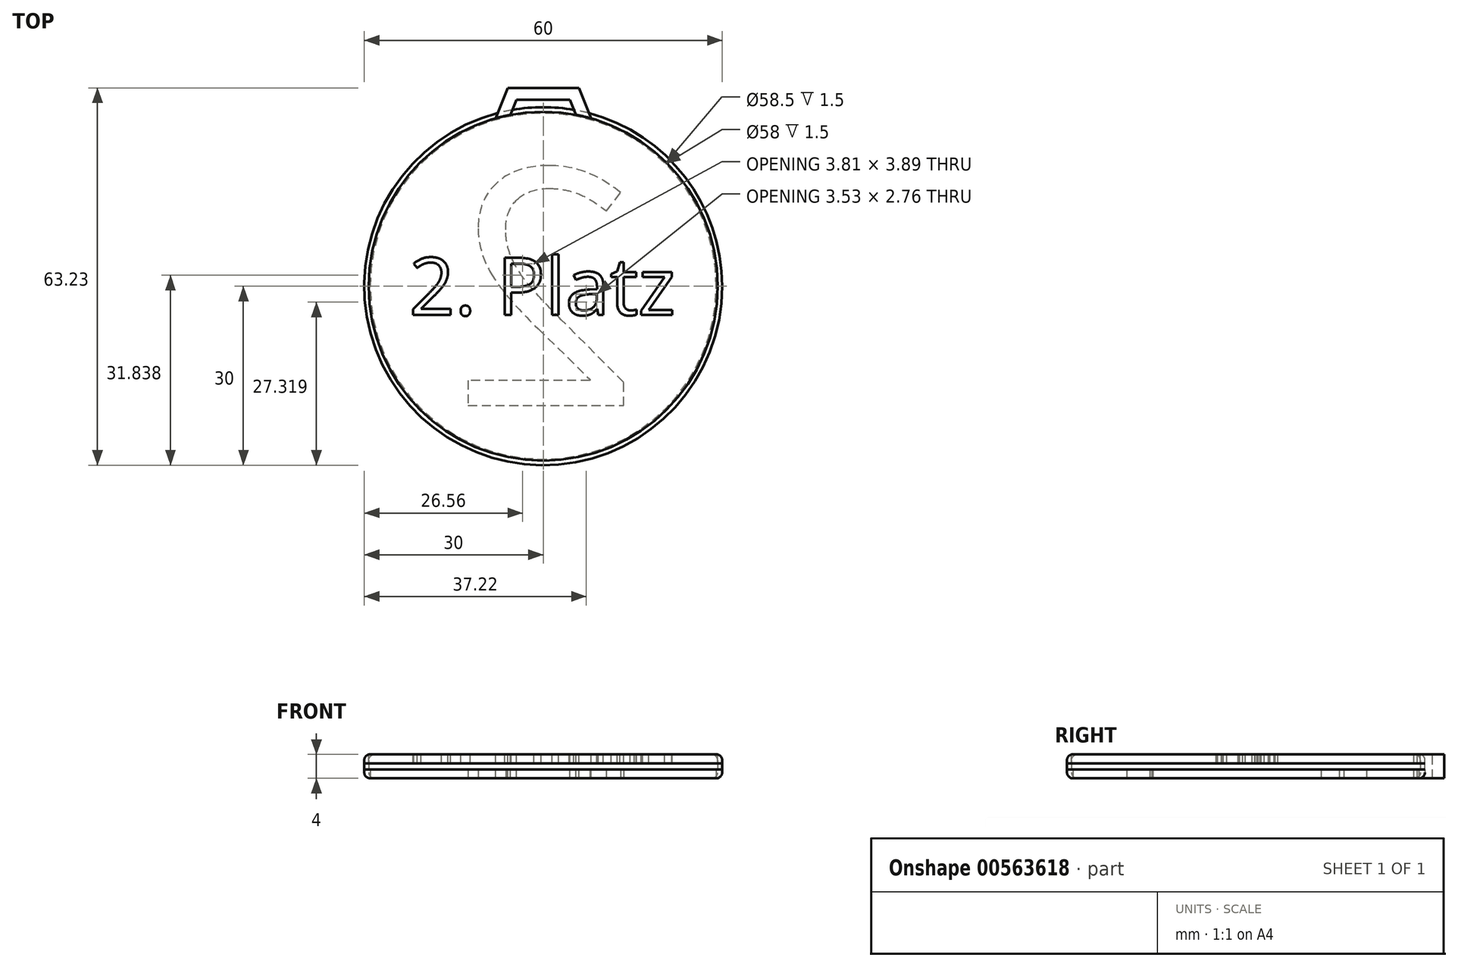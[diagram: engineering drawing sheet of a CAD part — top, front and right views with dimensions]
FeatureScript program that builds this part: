
annotation { "Feature Type Name" : "Feature", "Feature Type Description" : "" }
export const myFeature = defineFeature(function(context is Context, id is Id, definition is map)
    precondition{}
    {
        {
            var Q0;
            Q0=qCreatedBy(makeId("Top.planeOp"),FACE);
            var sketch = newSketch(context, id + "F0", { "sketchPlane" : qUnion([Q0])});
            skCircle(sketch, "E0", {"center": v(0, 0) * mm, "radius": 29.25 * mm});
            skSolve(sketch);
        }
        {
            var Q0;
            Q0 = qSketchRegion(id + "F0", true);
            extrude(context, id + "F1", {"entities" : qUnion([Q0]), "depth" : 4 * mm, "offsetDistance" : 25 * mm});
        }
        {
            var Q0;
            Q0=makeQuery(id+"F1.opExtrude","CAP_FACE",FACE,{"disambiguationData":[OSD([sQuery(id+"F0.wireOp",EDGE,"E0")])],"isStart":true});
            var sketch = newSketch(context, id + "F2", { "sketchPlane" : qUnion([Q0])});
            skText(sketch, "E1", { "text": "2", "fontName": "OpenSans-Regular.ttf"});
            skCircle(sketch, "E2", {"center": v(0, 0) * mm, "radius": 30 * mm});
            skCircle(sketch, "E3", {"center": v(0, 0) * mm, "radius": 29 * mm});
            const initialGuessF2  = {"E1": [-0.0162, -0.02, 1, 0, 0.04]};
            skSetInitialGuess(sketch, initialGuessF2);
            skSolve(sketch);
        }
        {
            var Q0;
            Q0 = qSketchRegion(id + "F2", true);
            var Q1;
            Q1=makeQuery(id+"F2.imprint","IMPRINT",FACE,{"disambiguationData":[TD([[makeQuery(id+"F2.imprint","IMPRINT",EDGE,{"derivedFrom":sQuery(id+"F2.wireOp",EDGE,"E1.sketch_text.stroke-0")}),-1.0]])]});
            extrude(context, id + "F3", {"entities" : qUnion([Q0, Q1]), "oppositeDirection" : true, "depth" : 1.5 * mm, "offsetDistance" : 25 * mm});
        }
        {
            var Q0;
            Q0=makeQuery(id+"F1.opExtrude","CAP_FACE",FACE,{"disambiguationData":[OSD([sQuery(id+"F0.wireOp",EDGE,"E0")])],"isStart":false});
            var sketch = newSketch(context, id + "F4", { "sketchPlane" : qUnion([Q0])});
            skText(sketch, "E4", { "text": "2. Platz", "fontName": "OpenSans-Regular.ttf"});
            skCircle(sketch, "E5", {"center": v(0, 0) * mm, "radius": 30 * mm});
            skCircle(sketch, "E6", {"center": v(0, 0) * mm, "radius": 29 * mm});
            const initialGuessF4  = {"E4": [-0.0225, -0.00483, 1, 0, 0.00966]};
            skSetInitialGuess(sketch, initialGuessF4);
            skSolve(sketch);
        }
        {
            var Q0;
            Q0=makeQuery(id+"F4.imprint","IMPRINT",FACE,{"disambiguationData":[TD([[makeQuery(id+"F4.imprint","IMPRINT",EDGE,{"derivedFrom":sQuery(id+"F4.wireOp",EDGE,"E4.sketch_text.stroke-0")}),-1.0]])]});
            var Q1;
            Q1=makeQuery(id+"F4.imprint","IMPRINT",FACE,{"disambiguationData":[TD([[makeQuery(id+"F4.imprint","IMPRINT",EDGE,{"derivedFrom":sQuery(id+"F4.wireOp",EDGE,"E4.sketch_text.stroke-20")}),-1.0]])]});
            var Q2;
            Q2=makeQuery(id+"F4.imprint","IMPRINT",FACE,{"disambiguationData":[TD([[makeQuery(id+"F4.imprint","IMPRINT",EDGE,{"derivedFrom":sQuery(id+"F4.wireOp",EDGE,"E4.sketch_text.stroke-28")}),-1.0]])]});
            var Q3;
            Q3=makeQuery(id+"F4.imprint","IMPRINT",FACE,{"disambiguationData":[TD([[makeQuery(id+"F4.imprint","IMPRINT",EDGE,{"derivedFrom":sQuery(id+"F4.wireOp",EDGE,"E4.sketch_text.stroke-43")}),-1.0]])]});
            var Q4;
            Q4=makeQuery(id+"F4.imprint","IMPRINT",FACE,{"disambiguationData":[TD([[makeQuery(id+"F4.imprint","IMPRINT",EDGE,{"derivedFrom":sQuery(id+"F4.wireOp",EDGE,"E4.sketch_text.stroke-47")}),-1.0]])]});
            var Q5;
            Q5=makeQuery(id+"F4.imprint","IMPRINT",FACE,{"disambiguationData":[TD([[makeQuery(id+"F4.imprint","IMPRINT",EDGE,{"derivedFrom":sQuery(id+"F4.wireOp",EDGE,"E4.sketch_text.stroke-74")}),-1.0]])]});
            var Q6;
            Q6=makeQuery(id+"F4.imprint","IMPRINT",FACE,{"disambiguationData":[TD([[makeQuery(id+"F4.imprint","IMPRINT",EDGE,{"derivedFrom":sQuery(id+"F4.wireOp",EDGE,"E4.sketch_text.stroke-93")}),-1.0]])]});
            var Q7;
            Q7=makeQuery(id+"F4.imprint","IMPRINT",FACE,{"disambiguationData":[TD([[makeQuery(id+"F4.imprint","IMPRINT",EDGE,{"derivedFrom":sQuery(id+"F4.wireOp",EDGE,"E5")}),1.0]])]});
            extrude(context, id + "F5", {"entities" : qUnion([Q0, Q1, Q2, Q3, Q4, Q5, Q6, Q7]), "oppositeDirection" : true, "depth" : 1.5 * mm, "offsetDistance" : 25 * mm});
        }
        {
            var Q0;
            Q0=qCreatedBy(makeId("Front.planeOp"),FACE);
            var sketch = newSketch(context, id + "F6", { "sketchPlane" : qUnion([Q0])});
            skLineSegment(sketch, "E7", {"start": v(0, 25) * mm, "end": v(0, -25) * mm, "construction": true});
            skSolve(sketch);
        }
        {
            var Q0;
            Q0=makeQuery(id+"F3.opExtrude","SWEPT_BODY",BODY,{"disambiguationData":[OSD([sQuery(id+"F2.wireOp",EDGE,"E1.sketch_text.stroke-0"),sQuery(id+"F2.wireOp",EDGE,"E1.sketch_text.stroke-1"),sQuery(id+"F2.wireOp",EDGE,"E1.sketch_text.stroke-2"),sQuery(id+"F2.wireOp",EDGE,"E1.sketch_text.stroke-3"),sQuery(id+"F2.wireOp",EDGE,"E1.sketch_text.stroke-4"),sQuery(id+"F2.wireOp",EDGE,"E1.sketch_text.stroke-5"),sQuery(id+"F2.wireOp",EDGE,"E1.sketch_text.stroke-6"),sQuery(id+"F2.wireOp",EDGE,"E1.sketch_text.stroke-7"),sQuery(id+"F2.wireOp",EDGE,"E1.sketch_text.stroke-8"),sQuery(id+"F2.wireOp",EDGE,"E1.sketch_text.stroke-9"),sQuery(id+"F2.wireOp",EDGE,"E1.sketch_text.stroke-10"),sQuery(id+"F2.wireOp",EDGE,"E1.sketch_text.stroke-11"),sQuery(id+"F2.wireOp",EDGE,"E1.sketch_text.stroke-12"),sQuery(id+"F2.wireOp",EDGE,"E1.sketch_text.stroke-13"),sQuery(id+"F2.wireOp",EDGE,"E1.sketch_text.stroke-14"),sQuery(id+"F2.wireOp",EDGE,"E1.sketch_text.stroke-15"),sQuery(id+"F2.wireOp",EDGE,"E1.sketch_text.stroke-16"),sQuery(id+"F2.wireOp",EDGE,"E1.sketch_text.stroke-17"),sQuery(id+"F2.wireOp",EDGE,"E1.sketch_text.stroke-18"),sQuery(id+"F2.wireOp",EDGE,"E1.sketch_text.stroke-19")])]});
            var Q1;
            Q1=sQuery(id+"F6.wireOp",EDGE,"E7");
            transform(context, id + "F7", {"entities" : qUnion([Q0]), "transformType" : TransformType.ROTATION, "transformAxis" : qUnion([Q1]), "angle" : 180 * degree, "makeCopy" : false});
        }
        {
            var Q0;
            Q0=makeQuery(id+"F5.opExtrude","CAP_FACE",FACE,{"disambiguationData":[OSD([sQuery(id+"F4.wireOp",EDGE,"E4.sketch_text.stroke-74"),sQuery(id+"F4.wireOp",EDGE,"E4.sketch_text.stroke-75"),sQuery(id+"F4.wireOp",EDGE,"E4.sketch_text.stroke-76"),sQuery(id+"F4.wireOp",EDGE,"E4.sketch_text.stroke-77"),sQuery(id+"F4.wireOp",EDGE,"E4.sketch_text.stroke-78"),sQuery(id+"F4.wireOp",EDGE,"E4.sketch_text.stroke-79"),sQuery(id+"F4.wireOp",EDGE,"E4.sketch_text.stroke-80"),sQuery(id+"F4.wireOp",EDGE,"E4.sketch_text.stroke-81"),sQuery(id+"F4.wireOp",EDGE,"E4.sketch_text.stroke-82"),sQuery(id+"F4.wireOp",EDGE,"E4.sketch_text.stroke-83"),sQuery(id+"F4.wireOp",EDGE,"E4.sketch_text.stroke-84"),sQuery(id+"F4.wireOp",EDGE,"E4.sketch_text.stroke-85"),sQuery(id+"F4.wireOp",EDGE,"E4.sketch_text.stroke-86"),sQuery(id+"F4.wireOp",EDGE,"E4.sketch_text.stroke-87"),sQuery(id+"F4.wireOp",EDGE,"E4.sketch_text.stroke-88"),sQuery(id+"F4.wireOp",EDGE,"E4.sketch_text.stroke-89"),sQuery(id+"F4.wireOp",EDGE,"E4.sketch_text.stroke-90"),sQuery(id+"F4.wireOp",EDGE,"E4.sketch_text.stroke-91"),sQuery(id+"F4.wireOp",EDGE,"E4.sketch_text.stroke-92")])],"isStart":false});
            var sketch = newSketch(context, id + "F8", { "sketchPlane" : qUnion([Q0])});
            skCircle(sketch, "E8", {"center": v(0, 0) * mm, "radius": 30 * mm});
            skSolve(sketch);
        }
        {
            var Q0;
            Q0 = qSketchRegion(id + "F8", true);
            extrude(context, id + "F9", {"entities" : qUnion([Q0]), "depth" : 1 * mm, "offsetDistance" : 25 * mm});
        }
        {
            var Q0;
            Q0=makeQuery(id+"F1.opExtrude","CAP_FACE",FACE,{"disambiguationData":[OSD([sQuery(id+"F0.wireOp",EDGE,"E0")])],"isStart":false});
            var sketch = newSketch(context, id + "F10", { "sketchPlane" : qUnion([Q0])});
            skLineSegment(sketch, "E9", {"start": v(-5.5, 28.73) * mm, "end": v(-4.5, 31.23) * mm});
            skLineSegment(sketch, "E10", {"start": v(-4.5, 31.23) * mm, "end": v(4.5, 31.23) * mm});
            skLineSegment(sketch, "E11", {"start": v(4.5, 31.23) * mm, "end": v(5.5, 28.73) * mm});
            skLineSegment(sketch, "E12", {"start": v(-8, 28.13) * mm, "end": v(-5.96, 33.23) * mm});
            skLineSegment(sketch, "E13", {"start": v(-5.96, 33.23) * mm, "end": v(5.96, 33.23) * mm});
            skLineSegment(sketch, "E14", {"start": v(5.96, 33.23) * mm, "end": v(8, 28.13) * mm});
            skArc(sketch, "E15", {"start": v(-8, 28.13) * mm, "mid": v(-6.76, 28.46) * mm, "end": v(-5.5, 28.73) * mm});
            skArc(sketch, "E16", {"start": v(5.5, 28.73) * mm, "mid": v(6.76, 28.46) * mm, "end": v(8, 28.13) * mm});
            skSolve(sketch);
        }
        {
            var Q0;
            Q0 = qSketchRegion(id + "F10", true);
            extrude(context, id + "F11", {"entities" : qUnion([Q0]), "oppositeDirection" : true, "depth" : 4 * mm, "offsetDistance" : 25 * mm});
        }
        {
            var Q0;
            Q0=makeQuery(id+"F3.opExtrude","SWEPT_BODY",BODY,{"disambiguationData":[OSD([sQuery(id+"F2.wireOp",EDGE,"E1.sketch_text.stroke-0"),sQuery(id+"F2.wireOp",EDGE,"E1.sketch_text.stroke-1"),sQuery(id+"F2.wireOp",EDGE,"E1.sketch_text.stroke-2"),sQuery(id+"F2.wireOp",EDGE,"E1.sketch_text.stroke-3"),sQuery(id+"F2.wireOp",EDGE,"E1.sketch_text.stroke-4"),sQuery(id+"F2.wireOp",EDGE,"E1.sketch_text.stroke-5"),sQuery(id+"F2.wireOp",EDGE,"E1.sketch_text.stroke-6"),sQuery(id+"F2.wireOp",EDGE,"E1.sketch_text.stroke-7"),sQuery(id+"F2.wireOp",EDGE,"E1.sketch_text.stroke-8"),sQuery(id+"F2.wireOp",EDGE,"E1.sketch_text.stroke-9"),sQuery(id+"F2.wireOp",EDGE,"E1.sketch_text.stroke-10"),sQuery(id+"F2.wireOp",EDGE,"E1.sketch_text.stroke-11"),sQuery(id+"F2.wireOp",EDGE,"E1.sketch_text.stroke-12"),sQuery(id+"F2.wireOp",EDGE,"E1.sketch_text.stroke-13"),sQuery(id+"F2.wireOp",EDGE,"E1.sketch_text.stroke-14"),sQuery(id+"F2.wireOp",EDGE,"E1.sketch_text.stroke-15"),sQuery(id+"F2.wireOp",EDGE,"E1.sketch_text.stroke-16"),sQuery(id+"F2.wireOp",EDGE,"E1.sketch_text.stroke-17"),sQuery(id+"F2.wireOp",EDGE,"E1.sketch_text.stroke-18"),sQuery(id+"F2.wireOp",EDGE,"E1.sketch_text.stroke-19")])]});
            var Q1;
            Q1=makeQuery(id+"F11.opExtrude","SWEPT_BODY",BODY,{"disambiguationData":[OSD([sQuery(id+"F10.wireOp",EDGE,"E9"),sQuery(id+"F10.wireOp",EDGE,"E10"),sQuery(id+"F10.wireOp",EDGE,"E11"),sQuery(id+"F10.wireOp",EDGE,"E12"),sQuery(id+"F10.wireOp",EDGE,"E13"),sQuery(id+"F10.wireOp",EDGE,"E14"),sQuery(id+"F10.wireOp",EDGE,"E15"),sQuery(id+"F10.wireOp",EDGE,"E16")])]});
            booleanBodies(context, id + "F12", {"operationType" : BooleanOperationType.UNION, "tools" : qUnion([Q0, Q1])});
        }
        {
            var Q0;
            Q0=makeQuery(id+"F11.opExtrude","CAP_EDGE",EDGE,{"disambiguationData":[OSD([sQuery(id+"F10.wireOp",EDGE,"E12")])],"isStart":true});
            var Q1;
            Q1=makeQuery(id+"F11.opExtrude","CAP_EDGE",EDGE,{"disambiguationData":[OSD([sQuery(id+"F10.wireOp",EDGE,"E13")])],"isStart":true});
            var Q2;
            Q2=makeQuery(id+"F11.opExtrude","CAP_EDGE",EDGE,{"disambiguationData":[OSD([sQuery(id+"F10.wireOp",EDGE,"E10")])],"isStart":true});
            var Q3;
            Q3=makeQuery(id+"F11.opExtrude","CAP_EDGE",EDGE,{"disambiguationData":[OSD([sQuery(id+"F10.wireOp",EDGE,"E14")])],"isStart":true});
            var Q4;
            Q4=makeQuery(id+"F11.opExtrude","CAP_EDGE",EDGE,{"disambiguationData":[OSD([sQuery(id+"F10.wireOp",EDGE,"E11")])],"isStart":true});
            var Q5;
            Q5=makeQuery(id+"F11.opExtrude","CAP_EDGE",EDGE,{"disambiguationData":[OSD([sQuery(id+"F10.wireOp",EDGE,"E9")])],"isStart":true});
            var Q6;
            Q6=makeQuery(id+"F11.opExtrude","CAP_EDGE",EDGE,{"disambiguationData":[OSD([sQuery(id+"F10.wireOp",EDGE,"E14")])],"isStart":false});
            var Q7;
            Q7=makeQuery(id+"F11.opExtrude","CAP_EDGE",EDGE,{"disambiguationData":[OSD([sQuery(id+"F10.wireOp",EDGE,"E11")])],"isStart":false});
            var Q8;
            Q8=makeQuery(id+"F11.opExtrude","CAP_EDGE",EDGE,{"disambiguationData":[OSD([sQuery(id+"F10.wireOp",EDGE,"E10")])],"isStart":false});
            var Q9;
            Q9=makeQuery(id+"F11.opExtrude","CAP_EDGE",EDGE,{"disambiguationData":[OSD([sQuery(id+"F10.wireOp",EDGE,"E9")])],"isStart":false});
            var Q10;
            Q10=makeQuery(id+"F11.opExtrude","CAP_EDGE",EDGE,{"disambiguationData":[OSD([sQuery(id+"F10.wireOp",EDGE,"E13")])],"isStart":false});
            var Q11;
            Q11=makeQuery(id+"F11.opExtrude","CAP_EDGE",EDGE,{"disambiguationData":[OSD([sQuery(id+"F10.wireOp",EDGE,"E12")])],"isStart":false});
            var Q12;
            Q12=makeQuery(id+"F11.opExtrude","SWEPT_EDGE",EDGE,{"disambiguationData":[OSD([sQuery(id+"F0.wireOp",EDGE,"E0"),sQuery(id+"F10.wireOp",EDGE,"E14"),sQuery(id+"F10.wireOp",EDGE,"E16")])]});
            var Q13;
            Q13=makeQuery(id+"F11.opExtrude","SWEPT_EDGE",EDGE,{"disambiguationData":[OSD([sQuery(id+"F0.wireOp",EDGE,"E0"),sQuery(id+"F10.wireOp",EDGE,"E12"),sQuery(id+"F10.wireOp",EDGE,"E15")])]});
            var Q14;
            Q14=makeQuery(id+"F1.opExtrude","CAP_EDGE",EDGE,{"disambiguationData":[OSD([sQuery(id+"F0.wireOp",EDGE,"E0")])],"isStart":false});
            var Q15;
            {var subQ1=sQuery(id+"F2.wireOp",EDGE,"E2");var subQ2=sQuery(id+"F10.wireOp",EDGE,"E9");Q15=makeQuery(id+"F12.opBoolean","SPLIT",EDGE,{"disambiguationData":[TD([makeQuery(id+"F11.opExtrude","SWEPT_FACE",FACE,{"disambiguationData":[OSD([subQ2])]})])],"derivedFrom":makeQuery(id+"F3.opExtrude","CAP_EDGE",EDGE,{"disambiguationData":[OSD([subQ1])],"isStart":true})});}
            var Q16;
            {var subQ0=sQuery(id+"F4.wireOp",EDGE,"E5");var subQ1=sQuery(id+"F10.wireOp",EDGE,"E12");Q16=makeQuery(id+"F12.opBoolean","SPLIT",EDGE,{"disambiguationData":[TD([makeQuery(id+"F11.opExtrude","SWEPT_FACE",FACE,{"disambiguationData":[OSD([subQ1])]})])],"derivedFrom":makeQuery(id+"F5.opExtrude","CAP_EDGE",EDGE,{"disambiguationData":[OSD([subQ0])],"isStart":true})});}
            var Q17;
            Q17=makeQuery(id+"F1.opExtrude","CAP_EDGE",EDGE,{"disambiguationData":[OSD([sQuery(id+"F0.wireOp",EDGE,"E0")])],"isStart":true});
            var Q18;
            {var subQ0=sQuery(id+"F2.wireOp",EDGE,"E2");var subQ2=sQuery(id+"F10.wireOp",EDGE,"E12");Q18=makeQuery(id+"F12.opBoolean","SPLIT",EDGE,{"disambiguationData":[TD([makeQuery(id+"F11.opExtrude","SWEPT_FACE",FACE,{"disambiguationData":[OSD([subQ2])]})])],"derivedFrom":makeQuery(id+"F3.opExtrude","CAP_EDGE",EDGE,{"disambiguationData":[OSD([subQ0])],"isStart":true})});}
            var Q19;
            {var subQ0=sQuery(id+"F4.wireOp",EDGE,"E5");var subQ2=sQuery(id+"F10.wireOp",EDGE,"E9");Q19=makeQuery(id+"F12.opBoolean","SPLIT",EDGE,{"disambiguationData":[TD([makeQuery(id+"F11.opExtrude","SWEPT_FACE",FACE,{"disambiguationData":[OSD([subQ2])]})])],"derivedFrom":makeQuery(id+"F5.opExtrude","CAP_EDGE",EDGE,{"disambiguationData":[OSD([subQ0])],"isStart":true})});}
            fillet(context, id + "F13", {"entities" : qUnion([Q0, Q1, Q2, Q3, Q4, Q5, Q6, Q7, Q8, Q9, Q10, Q11, Q12, Q13, Q14, Q15, Q16, Q17, Q18, Q19]), "radius" : 1 * mm, "allowEdgeOverflow" : false});
        }
        {
            var Q0;
            Q0=makeQuery(id+"F3.opExtrude","SWEPT_BODY",BODY,{"disambiguationData":[OSD([sQuery(id+"F2.wireOp",EDGE,"E1.sketch_text.stroke-0"),sQuery(id+"F2.wireOp",EDGE,"E1.sketch_text.stroke-1"),sQuery(id+"F2.wireOp",EDGE,"E1.sketch_text.stroke-2"),sQuery(id+"F2.wireOp",EDGE,"E1.sketch_text.stroke-3"),sQuery(id+"F2.wireOp",EDGE,"E1.sketch_text.stroke-4"),sQuery(id+"F2.wireOp",EDGE,"E1.sketch_text.stroke-5"),sQuery(id+"F2.wireOp",EDGE,"E1.sketch_text.stroke-6"),sQuery(id+"F2.wireOp",EDGE,"E1.sketch_text.stroke-7"),sQuery(id+"F2.wireOp",EDGE,"E1.sketch_text.stroke-8"),sQuery(id+"F2.wireOp",EDGE,"E1.sketch_text.stroke-9"),sQuery(id+"F2.wireOp",EDGE,"E1.sketch_text.stroke-10"),sQuery(id+"F2.wireOp",EDGE,"E1.sketch_text.stroke-11"),sQuery(id+"F2.wireOp",EDGE,"E1.sketch_text.stroke-12"),sQuery(id+"F2.wireOp",EDGE,"E1.sketch_text.stroke-13"),sQuery(id+"F2.wireOp",EDGE,"E1.sketch_text.stroke-14"),sQuery(id+"F2.wireOp",EDGE,"E1.sketch_text.stroke-15"),sQuery(id+"F2.wireOp",EDGE,"E1.sketch_text.stroke-16"),sQuery(id+"F2.wireOp",EDGE,"E1.sketch_text.stroke-17"),sQuery(id+"F2.wireOp",EDGE,"E1.sketch_text.stroke-18"),sQuery(id+"F2.wireOp",EDGE,"E1.sketch_text.stroke-19")])]});
            var Q1;
            Q1=makeQuery(id+"F1.opExtrude","SWEPT_BODY",BODY,{"disambiguationData":[OSD([sQuery(id+"F0.wireOp",EDGE,"E0")])]});
            booleanBodies(context, id + "F14", {"operationType" : BooleanOperationType.SUBTRACTION, "tools" : qUnion([Q0]), "targets" : qUnion([Q1]), "keepTools" : true});
        }
    });
